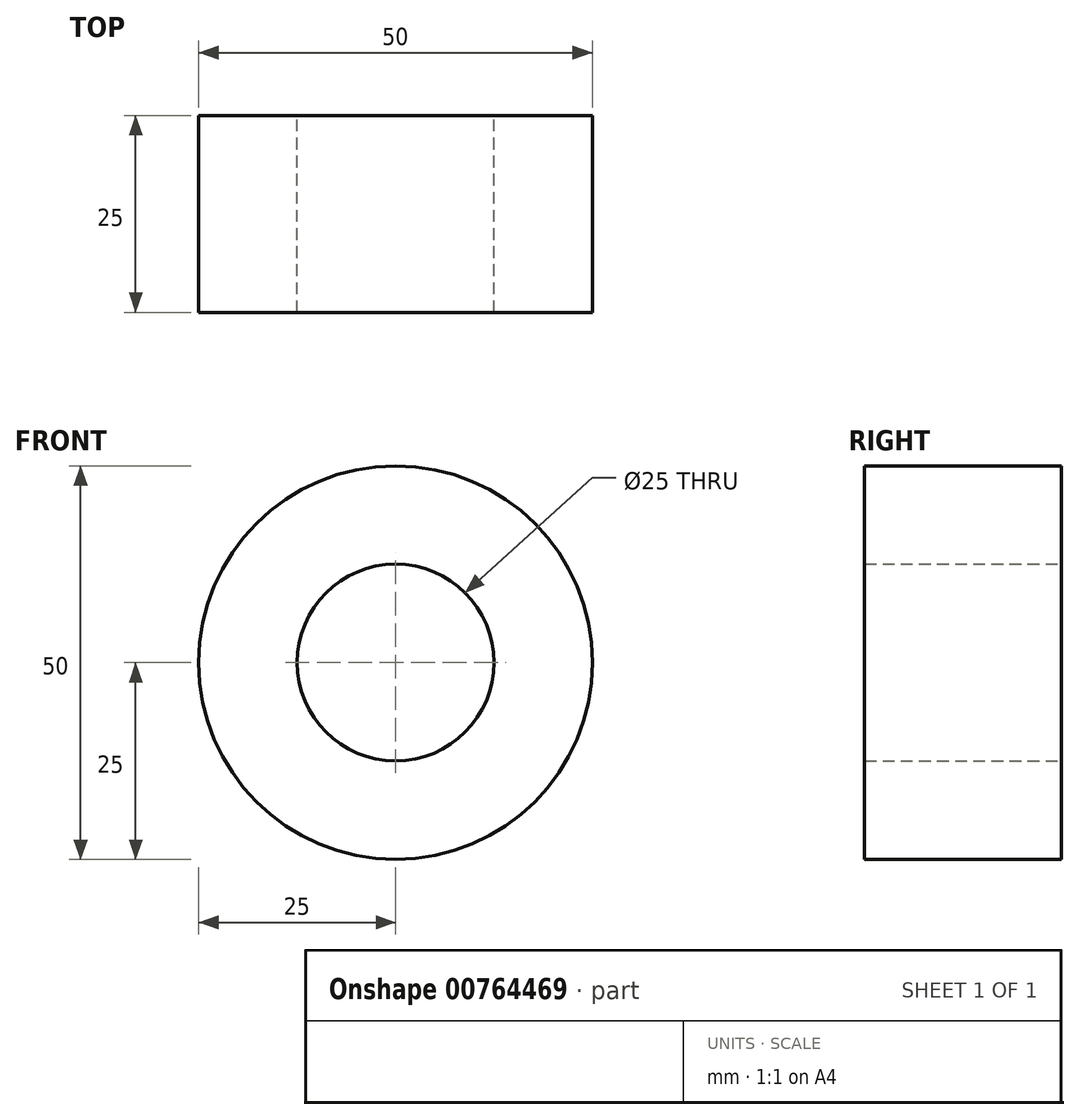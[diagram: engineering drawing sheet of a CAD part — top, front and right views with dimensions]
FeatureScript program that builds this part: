
annotation { "Feature Type Name" : "Feature", "Feature Type Description" : "" }
export const myFeature = defineFeature(function(context is Context, id is Id, definition is map)
    precondition{}
    {
        {
            var Q0;
            Q0=qCreatedBy(makeId("Front.planeOp"),FACE);
            var sketch = newSketch(context, id + "F0", { "sketchPlane" : qUnion([Q0])});
            skCircle(sketch, "E0", {"center": v(0, 0) * mm, "radius": 25 * mm});
            skSolve(sketch);
        }
        {
            var Q0;
            Q0 = qSketchRegion(id + "F0", true);
            extrude(context, id + "F1", {"entities" : qUnion([Q0]), "oppositeDirection" : true, "depth" : 25 * mm, "offsetDistance" : 25 * mm});
        }
        {
            var Q0;
            Q0=makeQuery(id+"F1.opExtrude","CAP_FACE",FACE,{"disambiguationData":[OSD([sQuery(id+"F0.wireOp",EDGE,"E0")])],"isStart":false});
            var sketch = newSketch(context, id + "F2", { "sketchPlane" : qUnion([Q0])});
            skCircle(sketch, "E1", {"center": v(0, 0) * mm, "radius": 12.5 * mm});
            skSolve(sketch);
        }
        {
            var Q0;
            Q0 = qSketchRegion(id + "F2", true);
            extrude(context, id + "F3", {"entities" : qUnion([Q0]), "operationType" : NewBodyOperationType.REMOVE, "oppositeDirection" : true, "depth" : 25 * mm, "offsetDistance" : 25 * mm});
        }
    });
